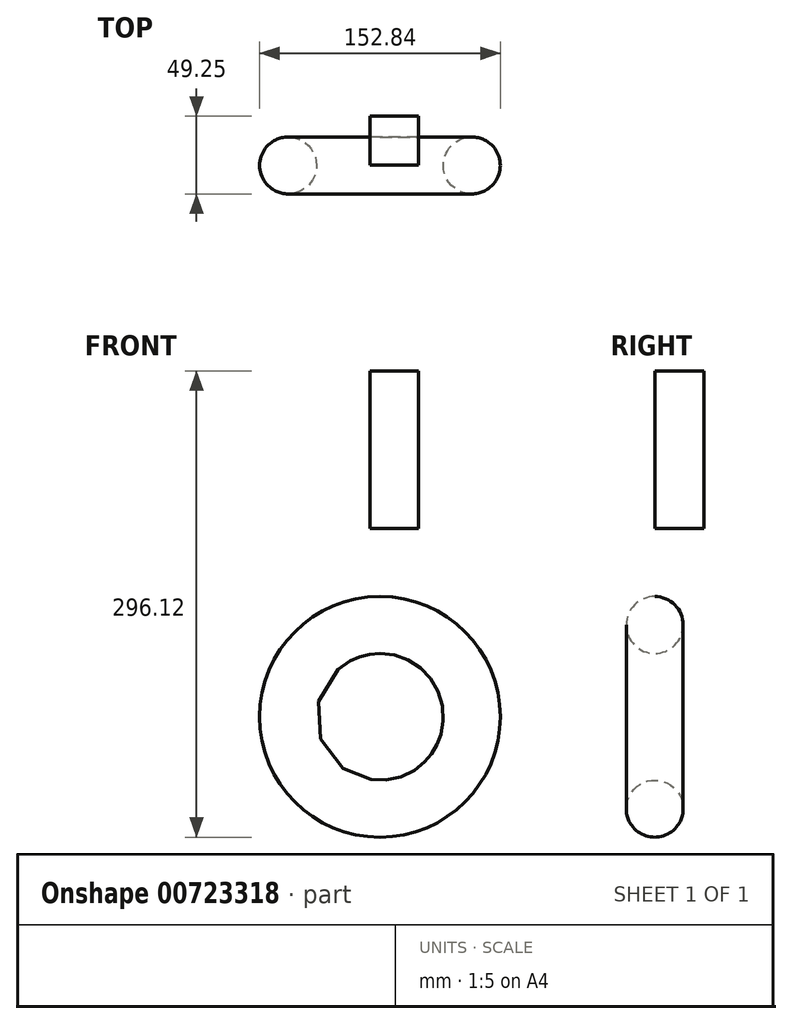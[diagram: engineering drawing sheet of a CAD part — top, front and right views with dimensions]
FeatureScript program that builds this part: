
annotation { "Feature Type Name" : "Feature", "Feature Type Description" : "" }
export const myFeature = defineFeature(function(context is Context, id is Id, definition is map)
    precondition{}
    {
        {
            var Q0;
            Q0=qCreatedBy(makeId("Top.planeOp"),FACE);
            var sketch = newSketch(context, id + "F0", { "sketchPlane" : qUnion([Q0])});
            skLineSegment(sketch, "E0", {"start": v(0, 48.14) * mm, "end": v(0, -49.34) * mm});
            skCircle(sketch, "E1", {"center": v(58.34, 7.56) * mm, "radius": 18.08 * mm});
            skSolve(sketch);
        }
        {
            var Q0;
            Q0=makeQuery(id+"F0.imprint","IMPRINT",FACE,{"disambiguationData":[TD([[makeQuery(id+"F0.imprint","IMPRINT",EDGE,{"derivedFrom":sQuery(id+"F0.wireOp",EDGE,"E1")}),1.0]])]});
            var Q1;
            Q1=sQuery(id+"F0.wireOp",EDGE,"E0");
            revolve(context, id + "F1", {"surfaceOperationType" : NewSurfaceOperationType.NEW, "entities" : qUnion([Q0]), "axis" : qUnion([Q1]), "revolveType" : RevolveType.FULL});
        }
        {
            var Q0;
            Q0=qCreatedBy(makeId("Top.planeOp"),FACE);
            cPlane(context, id + "F2", {"entities" : qUnion([Q0]), "cplaneType" : CPlaneType.OFFSET, "offset" : 119.7 * mm, "width" : 150 * mm, "height" : 150 * mm});
        }
        {
            var Q0;
            Q0=qCreatedBy(id+"F2.planeOp",FACE);
            var sketch = newSketch(context, id + "F3", { "sketchPlane" : qUnion([Q0])});
            skLineSegment(sketch, "E2.bottom", {"start": v(-6.3, 7.86) * mm, "end": v(24.57, 7.86) * mm});
            skLineSegment(sketch, "E2.top", {"start": v(-6.3, 38.74) * mm, "end": v(24.57, 38.74) * mm});
            skLineSegment(sketch, "E2.left", {"start": v(-6.3, 7.86) * mm, "end": v(-6.3, 38.74) * mm});
            skLineSegment(sketch, "E2.right", {"start": v(24.57, 7.86) * mm, "end": v(24.57, 38.74) * mm});
            skSolve(sketch);
        }
        {
            var Q0;
            Q0 = qSketchRegion(id + "F3", true);
            extrude(context, id + "F4", {"entities" : qUnion([Q0]), "depth" : 100 * mm, "offsetDistance" : 25 * mm});
        }
    });
